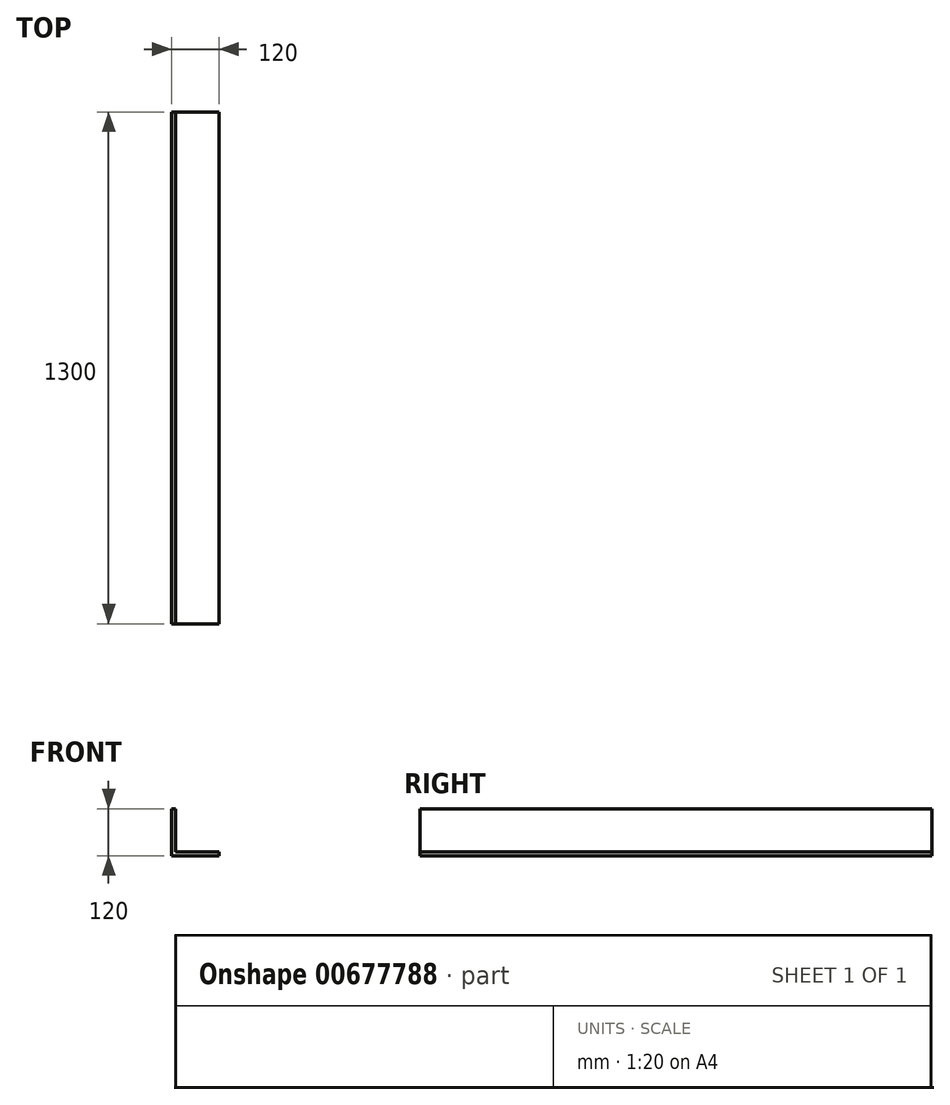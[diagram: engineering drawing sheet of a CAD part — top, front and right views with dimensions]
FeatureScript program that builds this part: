
annotation { "Feature Type Name" : "Feature", "Feature Type Description" : "" }
export const myFeature = defineFeature(function(context is Context, id is Id, definition is map)
    precondition{}
    {
        {
            var Q0;
            Q0=qCreatedBy(makeId("Front.planeOp"),FACE);
            var sketch = newSketch(context, id + "F0", { "sketchPlane" : qUnion([Q0])});
            skLineSegment(sketch, "E0.bottom", {"start": v(0, 0) * mm, "end": v(120, 0) * mm});
            skLineSegment(sketch, "E0.top", {"start": v(0, 120) * mm, "end": v(10, 120) * mm});
            skLineSegment(sketch, "E0.left", {"start": v(0, 0) * mm, "end": v(0, 120) * mm});
            skLineSegment(sketch, "E0.right", {"start": v(120, 0) * mm, "end": v(120, 10) * mm});
            skLineSegment(sketch, "E1.0", {"start": v(10, 10) * mm, "end": v(10, 120) * mm});
            skLineSegment(sketch, "E1.1", {"start": v(10, 10) * mm, "end": v(120, 10) * mm});
            skSolve(sketch);
        }
        {
            var Q0;
            Q0 = qSketchRegion(id + "F0", true);
            extrude(context, id + "F1", {"entities" : qUnion([Q0]), "depth" : 1300 * mm, "offsetDistance" : 25 * mm});
        }
    });
